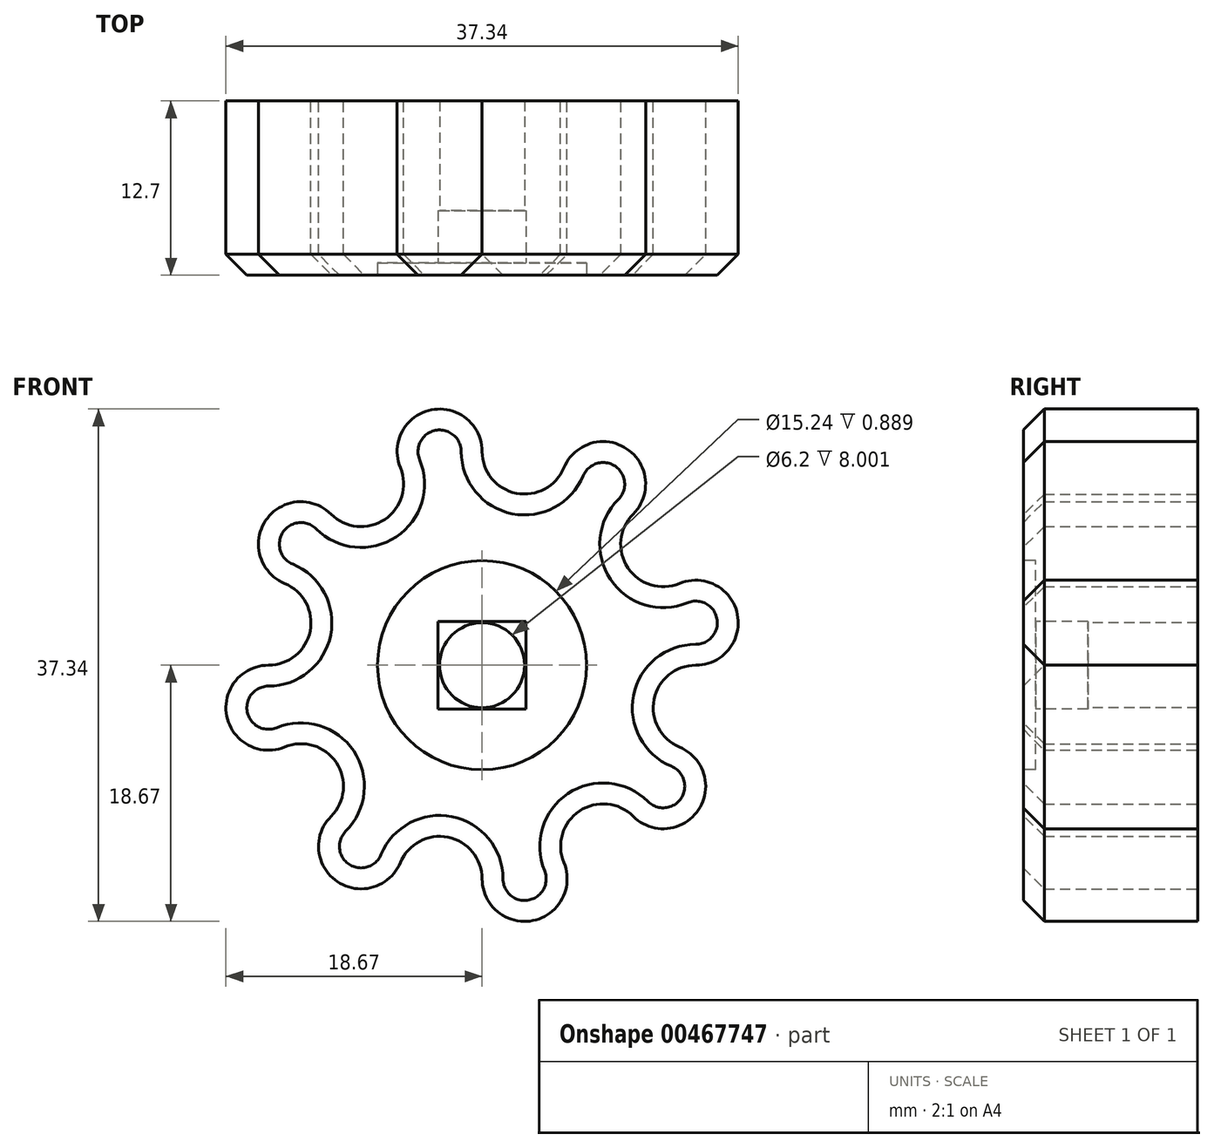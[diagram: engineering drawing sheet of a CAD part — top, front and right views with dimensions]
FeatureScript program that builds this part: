
annotation { "Feature Type Name" : "Feature", "Feature Type Description" : "" }
export const myFeature = defineFeature(function(context is Context, id is Id, definition is map)
    precondition{}
    {
        {
            var Q0;
            Q0=qCreatedBy(makeId("Front.planeOp"),FACE);
            var sketch = newSketch(context, id + "F0", { "sketchPlane" : qUnion([Q0])});
            skCircle(sketch, "E0", {"center": v(0, 0) * mm, "radius": 15.88 * mm, "construction": true});
            skLineSegment(sketch, "E1", {"start": v(0, 0) * mm, "end": v(-9.3, 22.45) * mm, "construction": true});
            skLineSegment(sketch, "E2", {"start": v(-16.83, 16.83) * mm, "end": v(0, 0) * mm, "construction": true});
            skLineSegment(sketch, "E3", {"start": v(0, 0) * mm, "end": v(-4.65, 23.37) * mm, "construction": true});
            skLineSegment(sketch, "E4", {"start": v(-12.76, 19.1) * mm, "end": v(0, 0) * mm, "construction": true});
            skArc(sketch, "E5", {"start": v(0, 15.57) * mm, "mid": v(-3.7, 18.6) * mm, "end": v(-5.96, 14.38) * mm});
            skArc(sketch, "E6", {"start": v(-11.21, 11.24) * mm, "mid": v(-7.1, 10.62) * mm, "end": v(-6.09, 14.66) * mm});
            skLineSegment(sketch, "E7", {"start": v(-11.23, 11.23) * mm, "end": v(0, 0) * mm});
            skLineSegment(sketch, "E8", {"start": v(0, 0) * mm, "end": v(0, 15.57) * mm});
            skSolve(sketch);
        }
        {
            var Q0;
            {var subQ0=sQuery(id+"F0.wireOp",EDGE,"E5");Q0=makeQuery(id+"F0.imprint","IMPRINT",FACE,{"disambiguationData":[TD([[makeQuery(id+"F0.imprint","IMPRINT",EDGE,{"derivedFrom":subQ0}),1.0]])]});}
            extrude(context, id + "F1", {"entities" : qUnion([Q0]), "depth" : 12.7 * mm});
        }
        {
            var Q0;
            Q0=makeQuery(id+"F1.opExtrude","SWEPT_BODY",BODY,{"disambiguationData":[OSD([sQuery(id+"F0.wireOp",EDGE,"E5"),sQuery(id+"F0.wireOp",EDGE,"E6"),sQuery(id+"F0.wireOp",EDGE,"E7"),sQuery(id+"F0.wireOp",EDGE,"E8")])]});
            var Q1;
            Q1=makeQuery(id+"F1.opExtrude","SWEPT_EDGE",EDGE,{"disambiguationData":[OSD([sQuery(id+"F0.wireOp",EDGE,"E7"),sQuery(id+"F0.wireOp",EDGE,"E8")])]});
            circularPattern(context, id + "F2", {"operationType" : NewBodyOperationType.ADD, "entities" : qUnion([Q0]), "axis" : qUnion([Q1]), "angle" : 360 * degree, "instanceCount" : 8, "equalSpace" : true});
        }
        {
            var Q0;
            Q0=makeQuery(id+"F1.opExtrude","CAP_EDGE",EDGE,{"disambiguationData":[OSD([sQuery(id+"F0.wireOp",EDGE,"E5")])],"isStart":false});
            chamfer(context, id + "F3", {"entities" : qUnion([Q0]), "width" : 1.52 * mm, "tangentPropagation" : true});
        }
        {
            var Q0;
            {var subQ0=makeQuery(id+"F1.opExtrude","CAP_FACE",FACE,{"disambiguationData":[OSD([sQuery(id+"F0.wireOp",EDGE,"E5"),sQuery(id+"F0.wireOp",EDGE,"E6"),sQuery(id+"F0.wireOp",EDGE,"E7"),sQuery(id+"F0.wireOp",EDGE,"E8")])],"isStart":false});Q0=makeQuery(id+"F2.boolean.opBoolean","MERGE",FACE,{"derivedFrom":[subQ0,makeQuery(id+"F2.opPattern","COPY",FACE,{"derivedFrom":subQ0,"instanceName":"1"}),makeQuery(id+"F2.opPattern","COPY",FACE,{"derivedFrom":subQ0,"instanceName":"2"}),makeQuery(id+"F2.opPattern","COPY",FACE,{"derivedFrom":subQ0,"instanceName":"3"}),makeQuery(id+"F2.opPattern","COPY",FACE,{"derivedFrom":subQ0,"instanceName":"4"}),makeQuery(id+"F2.opPattern","COPY",FACE,{"derivedFrom":subQ0,"instanceName":"5"}),makeQuery(id+"F2.opPattern","COPY",FACE,{"derivedFrom":subQ0,"instanceName":"6"}),makeQuery(id+"F2.opPattern","COPY",FACE,{"derivedFrom":subQ0,"instanceName":"7"})]});}
            var sketch = newSketch(context, id + "F4", { "sketchPlane" : qUnion([Q0])});
            skCircle(sketch, "E9", {"center": v(0, 0) * mm, "radius": 7.62 * mm});
            skSolve(sketch);
        }
        {
            var Q0;
            Q0=makeQuery(id+"F4.imprint","IMPRINT",FACE,{"disambiguationData":[TD([[makeQuery(id+"F4.imprint","IMPRINT",EDGE,{"derivedFrom":sQuery(id+"F4.wireOp",EDGE,"E9")}),1.0]])]});
            extrude(context, id + "F5", {"entities" : qUnion([Q0]), "operationType" : NewBodyOperationType.REMOVE, "oppositeDirection" : true, "depth" : 0.89 * mm});
        }
        {
            var Q0;
            Q0=makeQuery(id+"F5.boolean.opBoolean","COPY",FACE,{"derivedFrom":makeQuery(id+"F5.opExtrude","CAP_FACE",FACE,{"disambiguationData":[OSD([sQuery(id+"F4.wireOp",EDGE,"E9")])],"isStart":false})});
            var sketch = newSketch(context, id + "F6", { "sketchPlane" : qUnion([Q0])});
            skLineSegment(sketch, "E10.bottom", {"start": v(-3.2, 3.2) * mm, "end": v(3.2, 3.2) * mm});
            skLineSegment(sketch, "E10.top", {"start": v(-3.2, -3.2) * mm, "end": v(3.2, -3.2) * mm});
            skLineSegment(sketch, "E10.left", {"start": v(-3.2, 3.2) * mm, "end": v(-3.2, -3.2) * mm});
            skLineSegment(sketch, "E10.right", {"start": v(3.2, 3.2) * mm, "end": v(3.2, -3.2) * mm});
            skSolve(sketch);
        }
        {
            var Q0;
            Q0=makeQuery(id+"F6.imprint","IMPRINT",FACE,{"disambiguationData":[TD([[makeQuery(id+"F6.imprint","IMPRINT",EDGE,{"derivedFrom":sQuery(id+"F6.wireOp",EDGE,"E10.bottom")}),-1.0]])]});
            extrude(context, id + "F7", {"entities" : qUnion([Q0]), "operationType" : NewBodyOperationType.REMOVE, "oppositeDirection" : true, "depth" : 3.8 * mm});
        }
        {
            var Q0;
            Q0=makeQuery(id+"F7.boolean.opBoolean","COPY",FACE,{"derivedFrom":makeQuery(id+"F7.opExtrude","CAP_FACE",FACE,{"disambiguationData":[OSD([sQuery(id+"F6.wireOp",EDGE,"E10.bottom"),sQuery(id+"F6.wireOp",EDGE,"E10.top"),sQuery(id+"F6.wireOp",EDGE,"E10.left"),sQuery(id+"F6.wireOp",EDGE,"E10.right")])],"isStart":false})});
            var sketch = newSketch(context, id + "F8", { "sketchPlane" : qUnion([Q0])});
            skCircle(sketch, "E11", {"center": v(0, 0) * mm, "radius": 3.1 * mm});
            skSolve(sketch);
        }
        {
            var Q0;
            Q0=makeQuery(id+"F8.imprint","IMPRINT",FACE,{"disambiguationData":[TD([[makeQuery(id+"F8.imprint","IMPRINT",EDGE,{"derivedFrom":sQuery(id+"F8.wireOp",EDGE,"E11")}),1.0]])]});
            extrude(context, id + "F9", {"entities" : qUnion([Q0]), "operationType" : NewBodyOperationType.REMOVE, "endBound" : BoundingType.THROUGH_ALL, "oppositeDirection" : true, "depth" : 25.4 * mm});
        }
    });
